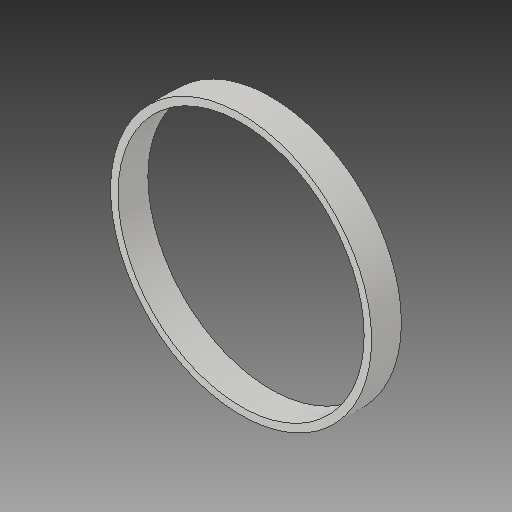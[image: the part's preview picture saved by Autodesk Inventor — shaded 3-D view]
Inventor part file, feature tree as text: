
AUTODESK INVENTOR PART (.ipt)
format: ipt  version: 2017 (Build 210142000, 142)  size: 99,840 bytes
history: native  units: in
note: dims shown in document units (in); Inventor stores cm internally (conversion verified against a paired STEP export)
features: extrude x1, shell x1, sketch x1
ambient origin geometry x8: Origin, YZ Plane, XZ Plane, XY Plane, X Axis, Y Axis, Z Axis, Center Point
bodies: Solid1 (feature_tree)
feature tree (3):
  extrude  "Extrusion1"  Depth=0.4in TaperAngle=0.0deg
  shell  "Shell1"  Thickness=0.1in
  sketch  "Sketch1"  dims[d0=3.5in d1=0.4in d2=0.0in d3=0.1in]
